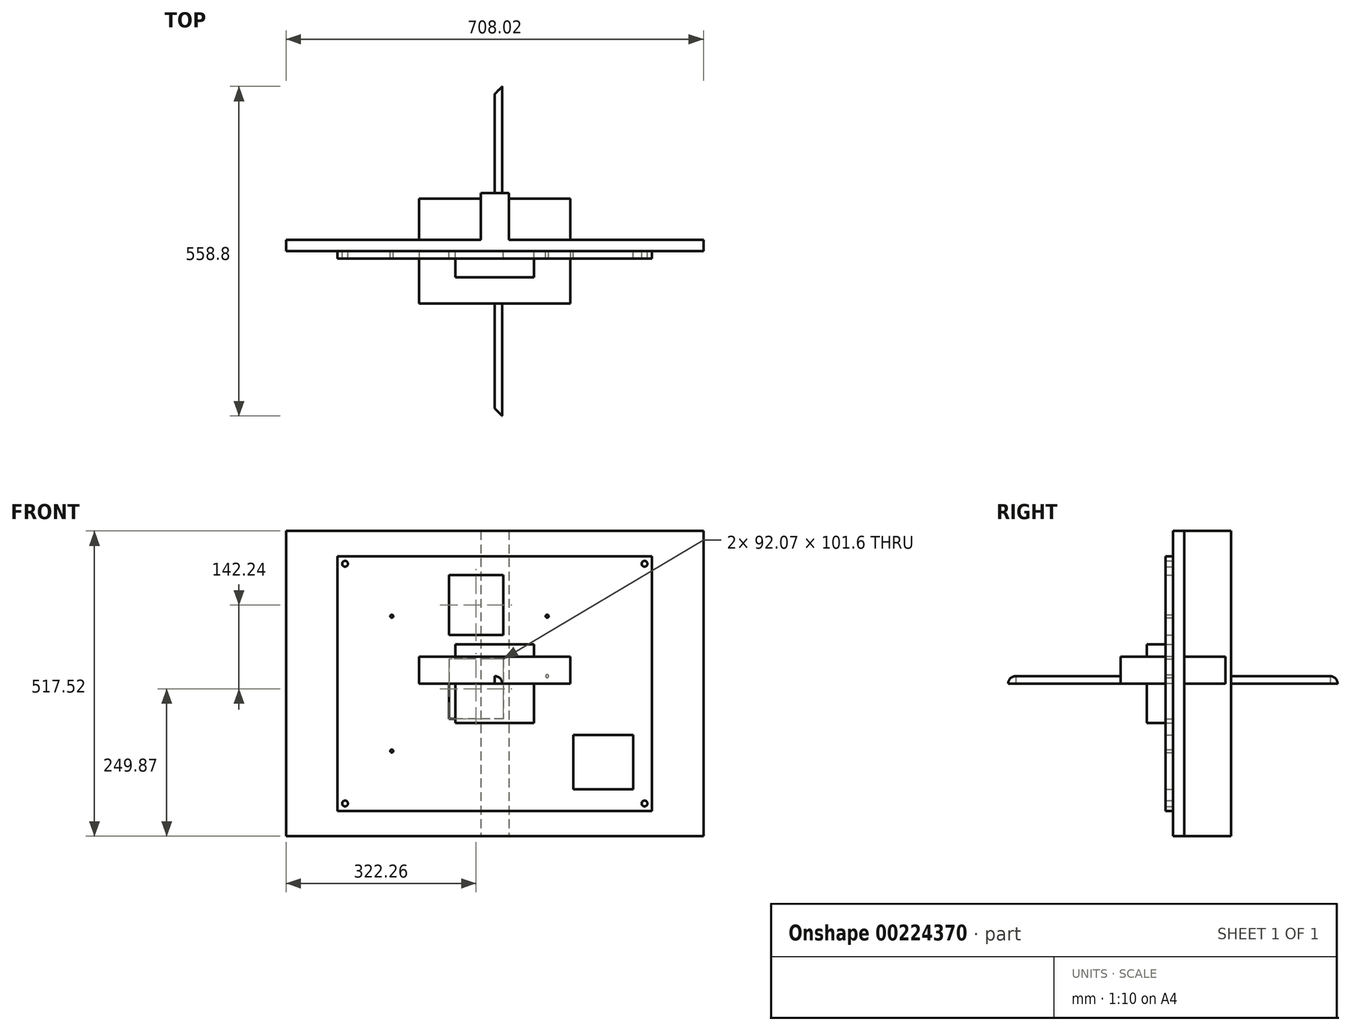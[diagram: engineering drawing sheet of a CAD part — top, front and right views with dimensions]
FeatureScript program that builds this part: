
annotation { "Feature Type Name" : "Feature", "Feature Type Description" : "" }
export const myFeature = defineFeature(function(context is Context, id is Id, definition is map)
    precondition{}
    {
        {
            var Q0;
            Q0=qCreatedBy(makeId("Top.planeOp"),FACE);
            var sketch = newSketch(context, id + "F0", { "sketchPlane" : qUnion([Q0])});
            skLineSegment(sketch, "E0.bottom", {"start": v(22, 43.5) * mm, "end": v(-22, 43.5) * mm});
            skLineSegment(sketch, "E0.top", {"start": v(22, -43.5) * mm, "end": v(-22, -43.5) * mm});
            skLineSegment(sketch, "E0.left", {"start": v(22, 43.5) * mm, "end": v(22, -43.5) * mm});
            skLineSegment(sketch, "E0.right", {"start": v(-22, 43.5) * mm, "end": v(-22, -43.5) * mm});
            skPoint(sketch, "E0.middle", {"position": v(0, 0) * mm});
            skSolve(sketch);
        }
        {
            var Q0;
            Q0=makeQuery(id+"F0.imprint","IMPRINT",FACE,{"disambiguationData":[TD([[makeQuery(id+"F0.imprint","IMPRINT",EDGE,{"derivedFrom":sQuery(id+"F0.wireOp",EDGE,"E0.bottom")}),1.0]])]});
            extrude(context, id + "F1", {"entities" : qUnion([Q0]), "depth" : 29 * mm});
        }
        {
            var Q0;
            Q0=qCreatedBy(makeId("Front.planeOp"),FACE);
            var sketch = newSketch(context, id + "F2", { "sketchPlane" : qUnion([Q0])});
            skLineSegment(sketch, "E1.bottom", {"start": v(57.15, 57.15) * mm, "end": v(-57.15, 57.15) * mm});
            skLineSegment(sketch, "E1.top", {"start": v(57.15, -57.15) * mm, "end": v(-57.15, -57.15) * mm});
            skLineSegment(sketch, "E1.left", {"start": v(57.15, 57.15) * mm, "end": v(57.15, -57.15) * mm});
            skLineSegment(sketch, "E1.right", {"start": v(-57.15, 57.15) * mm, "end": v(-57.15, -57.15) * mm});
            skPoint(sketch, "E1.middle", {"position": v(0, 0) * mm});
            skSolve(sketch);
        }
        {
            var Q0;
            Q0=makeQuery(id+"F2.imprint","IMPRINT",FACE,{"disambiguationData":[TD([[makeQuery(id+"F2.imprint","IMPRINT",EDGE,{"derivedFrom":sQuery(id+"F2.wireOp",EDGE,"E1.bottom")}),1.0]])]});
            extrude(context, id + "F3", {"entities" : qUnion([Q0]), "depth" : 5 / 406.4 * mm});
        }
        {
            var Q0;
            Q0=makeQuery(id+"F3.opExtrude","CAP_EDGE",EDGE,{"disambiguationData":[OSD([sQuery(id+"F2.wireOp",EDGE,"E1.bottom")])],"isStart":false});
            var Q1;
            Q1=makeQuery(id+"F3.opExtrude","CAP_EDGE",EDGE,{"disambiguationData":[OSD([sQuery(id+"F2.wireOp",EDGE,"E1.right")])],"isStart":false});
            var Q2;
            Q2=makeQuery(id+"F3.opExtrude","CAP_EDGE",EDGE,{"disambiguationData":[OSD([sQuery(id+"F2.wireOp",EDGE,"E1.left")])],"isStart":false});
            var Q3;
            Q3=makeQuery(id+"F3.opExtrude","CAP_EDGE",EDGE,{"disambiguationData":[OSD([sQuery(id+"F2.wireOp",EDGE,"E1.top")])],"isStart":false});
            fillet(context, id + "F4", {"entities" : qUnion([Q0, Q1, Q2, Q3]), "radius" : 5.08 * mm, "tangentPropagation" : true, "rho" : 0.1, "crossSection" : FilletCrossSection.CONIC, "allowEdgeOverflow" : false});
        }
        {
            var Q0;
            Q0=qCreatedBy(makeId("Top.planeOp"),FACE);
            var sketch = newSketch(context, id + "F5", { "sketchPlane" : qUnion([Q0])});
            skLineSegment(sketch, "E2.bottom", {"start": v(128.27, 88.9) * mm, "end": v(-128.27, 88.9) * mm});
            skLineSegment(sketch, "E2.top", {"start": v(128.27, -88.9) * mm, "end": v(-128.27, -88.9) * mm});
            skLineSegment(sketch, "E2.left", {"start": v(128.27, 88.9) * mm, "end": v(128.27, -88.9) * mm});
            skLineSegment(sketch, "E2.right", {"start": v(-128.27, 88.9) * mm, "end": v(-128.27, -88.9) * mm});
            skPoint(sketch, "E2.middle", {"position": v(0, 0) * mm});
            skSolve(sketch);
        }
        {
            var Q0;
            Q0=makeQuery(id+"F5.imprint","IMPRINT",FACE,{"disambiguationData":[TD([[makeQuery(id+"F5.imprint","IMPRINT",EDGE,{"derivedFrom":sQuery(id+"F5.wireOp",EDGE,"E2.bottom")}),1.0]])]});
            extrude(context, id + "F6", {"entities" : qUnion([Q0]), "depth" : 45.72 * mm});
        }
        {
            var Q0;
            Q0=qCreatedBy(makeId("Top.planeOp"),FACE);
            var sketch = newSketch(context, id + "F7", { "sketchPlane" : qUnion([Q0])});
            skLineSegment(sketch, "E3.bottom", {"start": v(67.5, 67.5) * mm, "end": v(-67.5, 67.5) * mm});
            skLineSegment(sketch, "E3.top", {"start": v(67.5, -67.5) * mm, "end": v(-67.5, -67.5) * mm});
            skLineSegment(sketch, "E3.left", {"start": v(67.5, 67.5) * mm, "end": v(67.5, -67.5) * mm});
            skLineSegment(sketch, "E3.right", {"start": v(-67.5, 67.5) * mm, "end": v(-67.5, -67.5) * mm});
            skPoint(sketch, "E3.middle", {"position": v(0, 0) * mm});
            skSolve(sketch);
        }
        {
            var Q0;
            Q0=makeQuery(id+"F7.imprint","IMPRINT",FACE,{"disambiguationData":[TD([[makeQuery(id+"F7.imprint","IMPRINT",EDGE,{"derivedFrom":sQuery(id+"F7.wireOp",EDGE,"E3.bottom")}),1.0]])]});
            extrude(context, id + "F8", {"entities" : qUnion([Q0]), "depth" : 28.3 * mm});
        }
        {
            var Q0;
            Q0=qCreatedBy(makeId("Front.planeOp"),FACE);
            var sketch = newSketch(context, id + "F9", { "sketchPlane" : qUnion([Q0])});
            skLineSegment(sketch, "E4.bottom", {"start": v(66.68, 66.68) * mm, "end": v(-66.68, 66.68) * mm});
            skLineSegment(sketch, "E4.top", {"start": v(66.68, -66.68) * mm, "end": v(-66.68, -66.68) * mm});
            skLineSegment(sketch, "E4.left", {"start": v(66.68, 66.68) * mm, "end": v(66.68, -66.68) * mm});
            skLineSegment(sketch, "E4.right", {"start": v(-66.68, 66.68) * mm, "end": v(-66.68, -66.68) * mm});
            skPoint(sketch, "E4.middle", {"position": v(0, 0) * mm});
            skSolve(sketch);
        }
        {
            var Q0;
            Q0 = qSketchRegion(id + "F9", true);
            extrude(context, id + "F10", {"entities" : qUnion([Q0]), "depth" : 44.45 * mm});
        }
        {
            var Q0;
            Q0=qCreatedBy(makeId("Front.planeOp"),FACE);
            var sketch = newSketch(context, id + "F11", { "sketchPlane" : qUnion([Q0])});
            skPoint(sketch, "E5.middle", {"position": v(0, 0) * mm});
            skLineSegment(sketch, "E6.bottom", {"start": v(254, 203.2) * mm, "end": v(-254, 203.2) * mm, "construction": true});
            skLineSegment(sketch, "E6.top", {"start": v(254, -203.2) * mm, "end": v(-254, -203.2) * mm, "construction": true});
            skLineSegment(sketch, "E6.left", {"start": v(254, 203.2) * mm, "end": v(254, -203.2) * mm, "construction": true});
            skLineSegment(sketch, "E6.right", {"start": v(-254, 203.2) * mm, "end": v(-254, -203.2) * mm, "construction": true});
            skLineSegment(sketch, "E7.bottom", {"start": v(266.7, 215.9) * mm, "end": v(-266.7, 215.9) * mm});
            skLineSegment(sketch, "E7.top", {"start": v(266.7, -215.9) * mm, "end": v(-266.7, -215.9) * mm});
            skLineSegment(sketch, "E7.left", {"start": v(266.7, 215.9) * mm, "end": v(266.7, -215.9) * mm});
            skLineSegment(sketch, "E7.right", {"start": v(-266.7, 215.9) * mm, "end": v(-266.7, -215.9) * mm});
            skPoint(sketch, "E8", {"position": v(-174.63, 114.3) * mm});
            skPoint(sketch, "E9", {"position": v(-174.63, -114.3) * mm});
            skPoint(sketch, "E10", {"position": v(88.9, 114.3) * mm});
            skPoint(sketch, "E11", {"position": v(88.9, 12.7) * mm});
            skLineSegment(sketch, "E12.bottom", {"start": v(14.29, 82.55) * mm, "end": v(-77.79, 82.55) * mm});
            skLineSegment(sketch, "E12.top", {"start": v(14.29, 184.15) * mm, "end": v(-77.79, 184.15) * mm});
            skLineSegment(sketch, "E12.left", {"start": v(14.29, 82.55) * mm, "end": v(14.29, 184.15) * mm});
            skLineSegment(sketch, "E12.right", {"start": v(-77.79, 82.55) * mm, "end": v(-77.79, 184.15) * mm});
            skPoint(sketch, "E12.middle", {"position": v(-31.75, 133.35) * mm});
            skLineSegment(sketch, "E13.bottom", {"start": v(14.29, 41.9) * mm, "end": v(-77.79, 41.9) * mm});
            skLineSegment(sketch, "E13.top", {"start": v(14.29, -59.7) * mm, "end": v(-77.79, -59.7) * mm});
            skLineSegment(sketch, "E13.left", {"start": v(14.29, 41.9) * mm, "end": v(14.29, -59.7) * mm});
            skLineSegment(sketch, "E13.right", {"start": v(-77.79, 41.9) * mm, "end": v(-77.79, -59.7) * mm});
            skPoint(sketch, "E13.middle", {"position": v(-31.75, -8.9) * mm});
            skLineSegment(sketch, "E14.bottom", {"start": v(234.95, -87.31) * mm, "end": v(133.35, -87.31) * mm});
            skLineSegment(sketch, "E14.top", {"start": v(234.95, -179.39) * mm, "end": v(133.35, -179.39) * mm});
            skLineSegment(sketch, "E14.left", {"start": v(234.95, -87.31) * mm, "end": v(234.95, -179.39) * mm});
            skLineSegment(sketch, "E14.right", {"start": v(133.35, -87.31) * mm, "end": v(133.35, -179.39) * mm});
            skPoint(sketch, "E14.middle", {"position": v(184.15, -133.35) * mm});
            skSolve(sketch);
        }
        {
            var Q0;
            Q0=makeQuery(id+"F11.imprint","IMPRINT",FACE,{"disambiguationData":[TD([[makeQuery(id+"F11.imprint","IMPRINT",EDGE,{"derivedFrom":sQuery(id+"F11.wireOp",EDGE,"E7.bottom")}),1.0]])]});
            extrude(context, id + "F12", {"entities" : qUnion([Q0]), "depth" : 12.7 * mm});
        }
        {
            var Q0;
            Q0=sQuery(id+"F11.wireOp",VERTEX,"E6.bottom.end");
            var Q1;
            Q1=sQuery(id+"F11.wireOp",VERTEX,"E6.left.start");
            var Q2;
            Q2=sQuery(id+"F11.wireOp",VERTEX,"E6.top.end");
            var Q3;
            Q3=sQuery(id+"F11.wireOp",VERTEX,"E6.top.start");
            var Q4;
            Q4=makeQuery(id+"F12.opExtrude","SWEPT_BODY",BODY,{"disambiguationData":[OSD([sQuery(id+"F11.wireOp",EDGE,"E7.bottom"),sQuery(id+"F11.wireOp",EDGE,"E7.top"),sQuery(id+"F11.wireOp",EDGE,"E7.left"),sQuery(id+"F11.wireOp",EDGE,"E7.right")])]});
            hole(context, id + "F13", {"style" : HoleStyle.SIMPLE, "endStyle" : HoleEndStyle.THROUGH, "oppositeDirection" : true, "holeDiameter" : 9.78 * mm, "locations" : qUnion([Q0, Q1, Q2, Q3]), "scope" : qUnion([Q4]), "isTappedThrough" : true});
        }
        {
            var Q0;
            Q0=qCreatedBy(makeId("Front.planeOp"),FACE);
            var sketch = newSketch(context, id + "F14", { "sketchPlane" : qUnion([Q0])});
            skLineSegment(sketch, "E15.bottom", {"start": v(354.01, 258.76) * mm, "end": v(-354.01, 258.76) * mm});
            skLineSegment(sketch, "E15.top", {"start": v(354.01, -258.76) * mm, "end": v(-354.01, -258.76) * mm});
            skLineSegment(sketch, "E15.left", {"start": v(354.01, 258.76) * mm, "end": v(354.01, -258.76) * mm});
            skLineSegment(sketch, "E15.right", {"start": v(-354.01, 258.76) * mm, "end": v(-354.01, -258.76) * mm});
            skPoint(sketch, "E15.middle", {"position": v(0, 0) * mm});
            skSolve(sketch);
        }
        {
            var Q0;
            Q0=makeQuery(id+"F14.imprint","IMPRINT",FACE,{"disambiguationData":[TD([[makeQuery(id+"F14.imprint","IMPRINT",EDGE,{"derivedFrom":sQuery(id+"F14.wireOp",EDGE,"E15.bottom")}),1.0]])]});
            extrude(context, id + "F15", {"entities" : qUnion([Q0]), "oppositeDirection" : true, "depth" : 19.05 * mm});
        }
        {
            var Q0;
            Q0=qCreatedBy(makeId("Front.planeOp"),FACE);
            var sketch = newSketch(context, id + "F16", { "sketchPlane" : qUnion([Q0])});
            skLineSegment(sketch, "E16.bottom", {"start": v(23.81, 258.76) * mm, "end": v(-23.81, 258.76) * mm});
            skLineSegment(sketch, "E16.top", {"start": v(23.81, -258.76) * mm, "end": v(-23.81, -258.76) * mm});
            skLineSegment(sketch, "E16.left", {"start": v(23.81, 258.76) * mm, "end": v(23.81, -258.76) * mm});
            skLineSegment(sketch, "E16.right", {"start": v(-23.81, 258.76) * mm, "end": v(-23.81, -258.76) * mm});
            skPoint(sketch, "E16.middle", {"position": v(0, 0) * mm});
            skSolve(sketch);
        }
        {
            var Q0;
            Q0=makeQuery(id+"F16.imprint","IMPRINT",FACE,{"disambiguationData":[TD([[makeQuery(id+"F16.imprint","IMPRINT",EDGE,{"derivedFrom":sQuery(id+"F16.wireOp",EDGE,"E16.bottom")}),1.0]])]});
            extrude(context, id + "F17", {"entities" : qUnion([Q0]), "oppositeDirection" : true, "depth" : 98.42 * mm});
        }
        {
            var Q0;
            Q0=sQuery(id+"F11.wireOp",VERTEX,"E8");
            var Q1;
            Q1=sQuery(id+"F11.wireOp",VERTEX,"E10");
            var Q2;
            Q2=sQuery(id+"F11.wireOp",VERTEX,"E11");
            var Q3;
            Q3=sQuery(id+"F11.wireOp",VERTEX,"E9");
            var Q4;
            Q4=makeQuery(id+"F12.opExtrude","SWEPT_BODY",BODY,{"disambiguationData":[OSD([sQuery(id+"F11.wireOp",EDGE,"E7.bottom"),sQuery(id+"F11.wireOp",EDGE,"E7.top"),sQuery(id+"F11.wireOp",EDGE,"E7.left"),sQuery(id+"F11.wireOp",EDGE,"E7.right")])]});
            hole(context, id + "F18", {"style" : HoleStyle.SIMPLE, "endStyle" : HoleEndStyle.THROUGH, "oppositeDirection" : true, "standardTappedOrClearance" : lookupTablePath({ "standard" : "ANSI", "fit" : "Close", "size" : "#10", "type" : "Clearance" }), "standardBlindInLast" : lookupTablePath({ "fit" : "Close", "standard" : "ANSI", "size" : "#10", "type" : "Clearance" }), "holeDiameter" : 4.98 * mm, "locations" : qUnion([Q0, Q1, Q2, Q3]), "scope" : qUnion([Q4]), "isTappedThrough" : true});
        }
        {
            var Q0;
            Q0=qCreatedBy(makeId("Right.planeOp"),FACE);
            var sketch = newSketch(context, id + "F19", { "sketchPlane" : qUnion([Q0])});
            skPoint(sketch, "E17", {"position": v(-266.7, 0) * mm});
            skLineSegment(sketch, "E18", {"start": v(-266.7, 0) * mm, "end": v(-266.7, 25.4) * mm, "construction": true});
            skPoint(sketch, "E19", {"position": v(-215.9, 0) * mm});
            skLineSegment(sketch, "E20", {"start": v(-215.9, 0) * mm, "end": v(-215.9, 25.4) * mm, "construction": true});
            skSolve(sketch);
        }
        {
            var Q0;
            Q0=sQuery(id+"F19.wireOp",EDGE,"E18");
            cPlane(context, id + "F20", {"entities" : qUnion([Q0]), "cplaneType" : CPlaneType.LINE_ANGLE, "offset" : 25.4 * mm, "angle" : 45 * degree, "width" : 152.4 * mm, "height" : 152.4 * mm});
        }
        {
            var Q0;
            Q0=sQuery(id+"F19.wireOp",EDGE,"E20");
            cPlane(context, id + "F21", {"entities" : qUnion([Q0]), "cplaneType" : CPlaneType.LINE_ANGLE, "offset" : 25.4 * mm, "angle" : 45 * degree, "width" : 152.4 * mm, "height" : 152.4 * mm});
        }
        {
            var Q0;
            Q0=qCreatedBy(makeId("Front.planeOp"),FACE);
            var sketch = newSketch(context, id + "F22", { "sketchPlane" : qUnion([Q0])});
            skLineSegment(sketch, "E21.bottom", {"start": v(0, 0) * mm, "end": v(12.7, 0) * mm});
            skLineSegment(sketch, "E21.top", {"start": v(0, 12.7) * mm, "end": v(0, 12.7) * mm});
            skLineSegment(sketch, "E21.left", {"start": v(0, 0) * mm, "end": v(0, 12.7) * mm});
            skLineSegment(sketch, "E21.right", {"start": v(12.7, 0) * mm, "end": v(12.7, 0) * mm});
            skPoint(sketch, "E22.visualSharp", {"position": v(12.7, 12.7) * mm});
            skArc(sketch, "E22.filletArc", {"start": v(12.7, 0) * mm, "mid": v(8.98, 8.98) * mm, "end": v(0, 12.7) * mm});
            skSolve(sketch);
        }
        {
            var Q0;
            Q0=makeQuery(id+"F22.imprint","IMPRINT",FACE,{"disambiguationData":[TD([[makeQuery(id+"F22.imprint","IMPRINT",EDGE,{"derivedFrom":sQuery(id+"F22.wireOp",EDGE,"E21.bottom")}),1.0]])]});
            var Q1;
            Q1=qCreatedBy(id+"F21.planeOp",FACE);
            extrude(context, id + "F23", {"entities" : qUnion([Q0]), "endBound" : BoundingType.UP_TO_SURFACE, "endBoundEntityFace" : qUnion([Q1]), "depth" : 25.4 * mm});
        }
        {
            var Q0;
            Q0=makeQuery(id+"F23.opExtrude","SWEPT_BODY",BODY,{"disambiguationData":[OSD([sQuery(id+"F22.wireOp",EDGE,"E21.bottom"),sQuery(id+"F22.wireOp",EDGE,"E21.left"),sQuery(id+"F22.wireOp",EDGE,"E22.filletArc")])]});
            var Q1;
            Q1=qCreatedBy(makeId("Front.planeOp"),FACE);
            mirror(context, id + "F24", {"operationType" : NewBodyOperationType.ADD, "entities" : qUnion([Q0]), "mirrorPlane" : qUnion([Q1])});
        }
        {
            var Q0;
            Q0=makeQuery(id+"F22.imprint","IMPRINT",FACE,{"disambiguationData":[TD([[makeQuery(id+"F22.imprint","IMPRINT",EDGE,{"derivedFrom":sQuery(id+"F22.wireOp",EDGE,"E21.bottom")}),1.0]])]});
            var Q1;
            Q1=qCreatedBy(id+"F20.planeOp",FACE);
            extrude(context, id + "F25", {"entities" : qUnion([Q0]), "endBound" : BoundingType.UP_TO_SURFACE, "endBoundEntityFace" : qUnion([Q1]), "depth" : 25.4 * mm});
        }
        {
            var Q0;
            Q0=makeQuery(id+"F25.opExtrude","SWEPT_BODY",BODY,{"disambiguationData":[OSD([sQuery(id+"F22.wireOp",EDGE,"E21.bottom"),sQuery(id+"F22.wireOp",EDGE,"E21.left"),sQuery(id+"F22.wireOp",EDGE,"E22.filletArc")])]});
            var Q1;
            Q1=qCreatedBy(makeId("Front.planeOp"),FACE);
            mirror(context, id + "F26", {"operationType" : NewBodyOperationType.ADD, "entities" : qUnion([Q0]), "mirrorPlane" : qUnion([Q1])});
        }
    });
